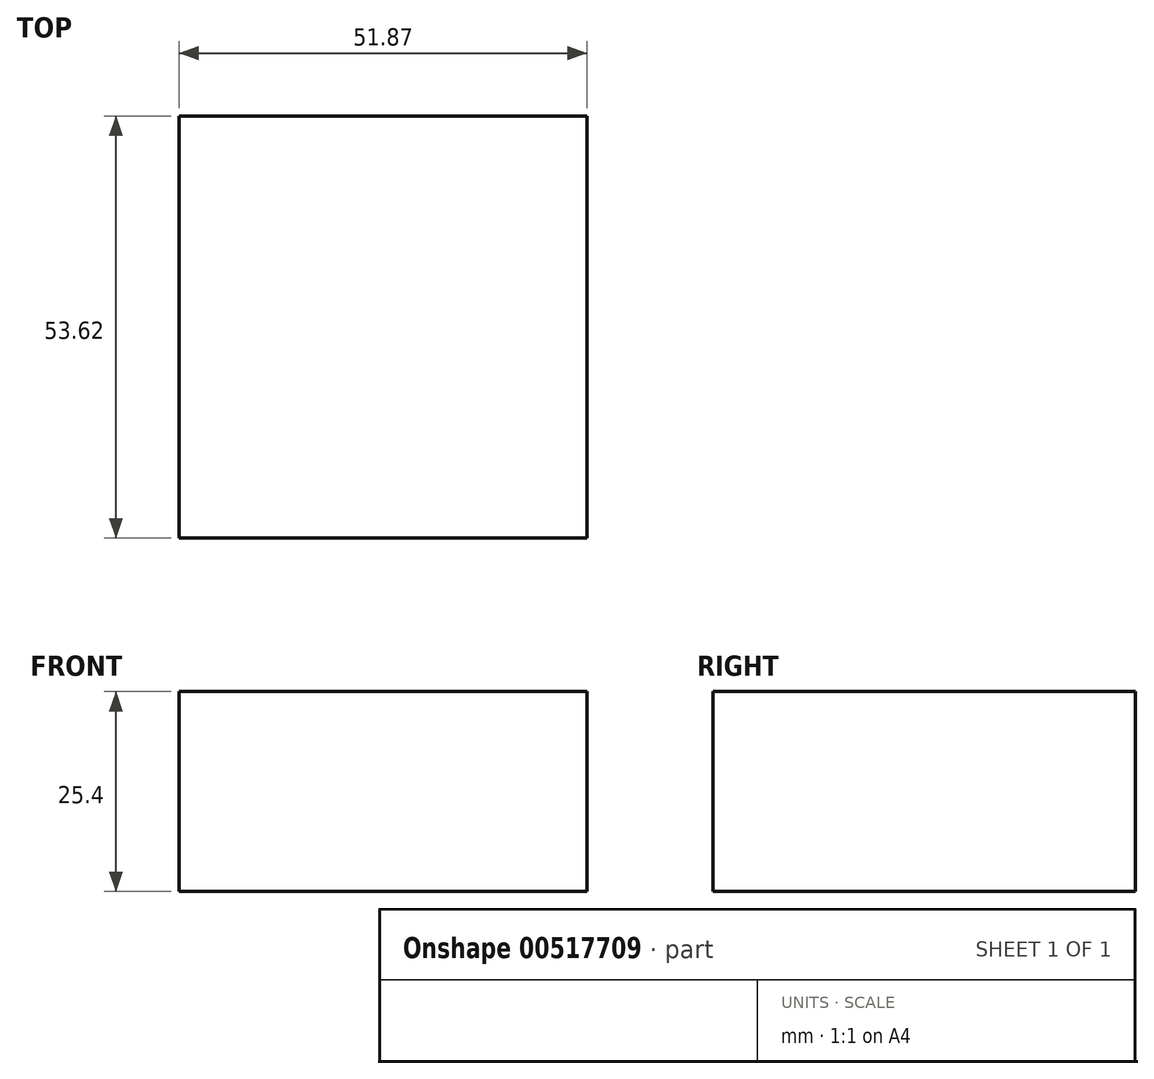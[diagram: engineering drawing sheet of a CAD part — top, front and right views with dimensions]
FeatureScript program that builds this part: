
annotation { "Feature Type Name" : "Feature", "Feature Type Description" : "" }
export const myFeature = defineFeature(function(context is Context, id is Id, definition is map)
    precondition{}
    {
        {
            var Q0;
            Q0=qCreatedBy(makeId("Top.planeOp"),FACE);
            var sketch = newSketch(context, id + "F0", { "sketchPlane" : qUnion([Q0])});
            skLineSegment(sketch, "E0.bottom", {"start": v(0, 0) * mm, "end": v(51.87, 0) * mm});
            skLineSegment(sketch, "E0.top", {"start": v(0, 53.62) * mm, "end": v(51.87, 53.62) * mm});
            skLineSegment(sketch, "E0.left", {"start": v(0, 0) * mm, "end": v(0, 53.62) * mm});
            skLineSegment(sketch, "E0.right", {"start": v(51.87, 0) * mm, "end": v(51.87, 53.62) * mm});
            skSolve(sketch);
        }
        {
            var Q0;
            Q0 = qConstructionFilter(qBodyType(qCreatedBy(id + "F0" ,EDGE), BodyType.WIRE), ConstructionObject.NO);
            extrude(context, id + "F1", {"bodyType" : ToolBodyType.SURFACE, "surfaceEntities" : qUnion([Q0]), "depth" : 25.4 * mm, "offsetDistance" : 25.4 * mm});
        }
    });
